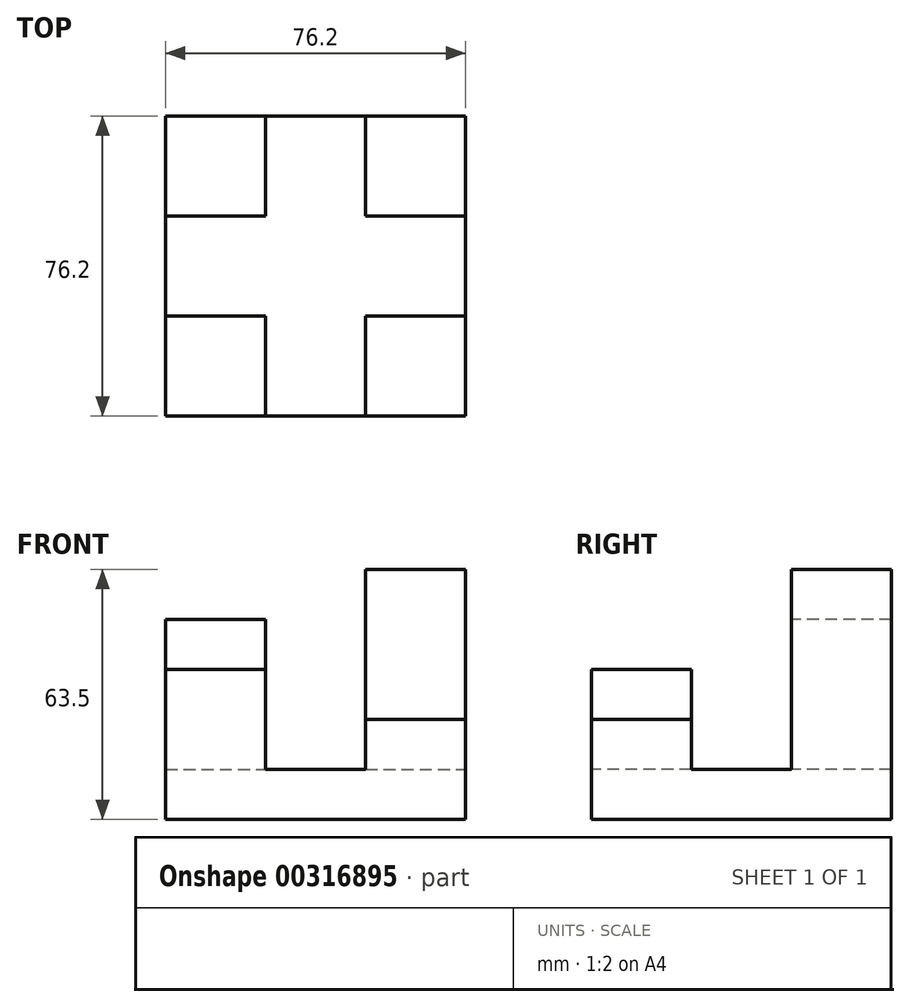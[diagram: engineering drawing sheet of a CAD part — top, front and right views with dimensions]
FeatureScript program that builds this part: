
annotation { "Feature Type Name" : "Feature", "Feature Type Description" : "" }
export const myFeature = defineFeature(function(context is Context, id is Id, definition is map)
    precondition{}
    {
        {
            var Q0;
            Q0=qCreatedBy(makeId("Top.planeOp"),FACE);
            var sketch = newSketch(context, id + "F0", { "sketchPlane" : qUnion([Q0])});
            skLineSegment(sketch, "E0", {"start": v(17.81, 51.18) * mm, "end": v(-58.39, 51.18) * mm});
            skLineSegment(sketch, "E1", {"start": v(-58.39, 51.18) * mm, "end": v(-58.39, -25.02) * mm});
            skLineSegment(sketch, "E2", {"start": v(-58.39, -25.02) * mm, "end": v(17.81, -25.02) * mm});
            skLineSegment(sketch, "E3", {"start": v(17.81, -25.02) * mm, "end": v(17.81, 51.18) * mm});
            skSolve(sketch);
        }
        {
            var Q0;
            Q0=makeQuery(id+"F0.imprint","IMPRINT",FACE,{"disambiguationData":[TD([[makeQuery(id+"F0.imprint","IMPRINT",EDGE,{"derivedFrom":sQuery(id+"F0.wireOp",EDGE,"E0")}),1.0]])]});
            extrude(context, id + "F1", {"entities" : qUnion([Q0]), "depth" : 12.7 * mm});
        }
        {
            var Q0;
            Q0=makeQuery(id+"F1.opExtrude","CAP_FACE",FACE,{"disambiguationData":[OSD([sQuery(id+"F0.wireOp",EDGE,"E0"),sQuery(id+"F0.wireOp",EDGE,"E1"),sQuery(id+"F0.wireOp",EDGE,"E2"),sQuery(id+"F0.wireOp",EDGE,"E3")])],"isStart":false});
            var sketch = newSketch(context, id + "F2", { "sketchPlane" : qUnion([Q0])});
            skLineSegment(sketch, "E4", {"start": v(-58.39, 25.78) * mm, "end": v(-32.99, 25.78) * mm});
            skLineSegment(sketch, "E5", {"start": v(-32.99, 25.78) * mm, "end": v(-32.99, 51.18) * mm});
            skLineSegment(sketch, "E6", {"start": v(-32.99, 51.18) * mm, "end": v(-58.39, 51.18) * mm});
            skLineSegment(sketch, "E7", {"start": v(-58.39, 51.18) * mm, "end": v(-58.39, 25.78) * mm});
            skLineSegment(sketch, "E8", {"start": v(-58.39, 0.38) * mm, "end": v(-32.99, 0.38) * mm});
            skLineSegment(sketch, "E9", {"start": v(-32.99, 0.38) * mm, "end": v(-32.99, -25.02) * mm});
            skLineSegment(sketch, "E10", {"start": v(-58.39, -25.02) * mm, "end": v(-58.39, 0.38) * mm});
            skLineSegment(sketch, "E11", {"start": v(-32.99, -25.02) * mm, "end": v(-58.39, -25.02) * mm});
            skLineSegment(sketch, "E12", {"start": v(-7.59, -25.02) * mm, "end": v(-7.59, 0.38) * mm});
            skLineSegment(sketch, "E13", {"start": v(-7.59, 0.38) * mm, "end": v(17.81, 0.38) * mm});
            skLineSegment(sketch, "E14", {"start": v(17.81, 0.38) * mm, "end": v(17.81, -25.02) * mm});
            skLineSegment(sketch, "E15", {"start": v(17.81, -25.02) * mm, "end": v(-7.59, -25.02) * mm});
            skLineSegment(sketch, "E16", {"start": v(-7.59, 51.18) * mm, "end": v(-7.59, 25.78) * mm});
            skLineSegment(sketch, "E17", {"start": v(-7.59, 25.78) * mm, "end": v(17.81, 25.78) * mm});
            skLineSegment(sketch, "E18", {"start": v(17.81, 25.78) * mm, "end": v(17.81, 51.18) * mm});
            skLineSegment(sketch, "E19", {"start": v(-7.59, 51.18) * mm, "end": v(17.81, 51.18) * mm});
            skSolve(sketch);
        }
        {
            var Q0;
            Q0=makeQuery(id+"F2.imprint","IMPRINT",FACE,{"disambiguationData":[TD([[makeQuery(id+"F2.imprint","IMPRINT",EDGE,{"derivedFrom":sQuery(id+"F2.wireOp",EDGE,"E4")}),1.0]])]});
            extrude(context, id + "F3", {"entities" : qUnion([Q0]), "operationType" : NewBodyOperationType.ADD, "depth" : 38.1 * mm});
        }
        {
            var Q0;
            Q0=makeQuery(id+"F2.imprint","IMPRINT",FACE,{"disambiguationData":[TD([[makeQuery(id+"F2.imprint","IMPRINT",EDGE,{"derivedFrom":sQuery(id+"F2.wireOp",EDGE,"E8")}),-1.0]])]});
            extrude(context, id + "F4", {"entities" : qUnion([Q0]), "operationType" : NewBodyOperationType.ADD, "depth" : 25.4 * mm});
        }
        {
            var Q0;
            Q0=makeQuery(id+"F2.imprint","IMPRINT",FACE,{"disambiguationData":[TD([[makeQuery(id+"F2.imprint","IMPRINT",EDGE,{"derivedFrom":sQuery(id+"F2.wireOp",EDGE,"E12")}),-1.0]])]});
            extrude(context, id + "F5", {"entities" : qUnion([Q0]), "operationType" : NewBodyOperationType.ADD, "depth" : 12.7 * mm});
        }
        {
            var Q0;
            Q0=makeQuery(id+"F2.imprint","IMPRINT",FACE,{"disambiguationData":[TD([[makeQuery(id+"F2.imprint","IMPRINT",EDGE,{"derivedFrom":sQuery(id+"F2.wireOp",EDGE,"E16")}),1.0]])]});
            extrude(context, id + "F6", {"entities" : qUnion([Q0]), "operationType" : NewBodyOperationType.ADD, "depth" : 50.8 * mm});
        }
    });
